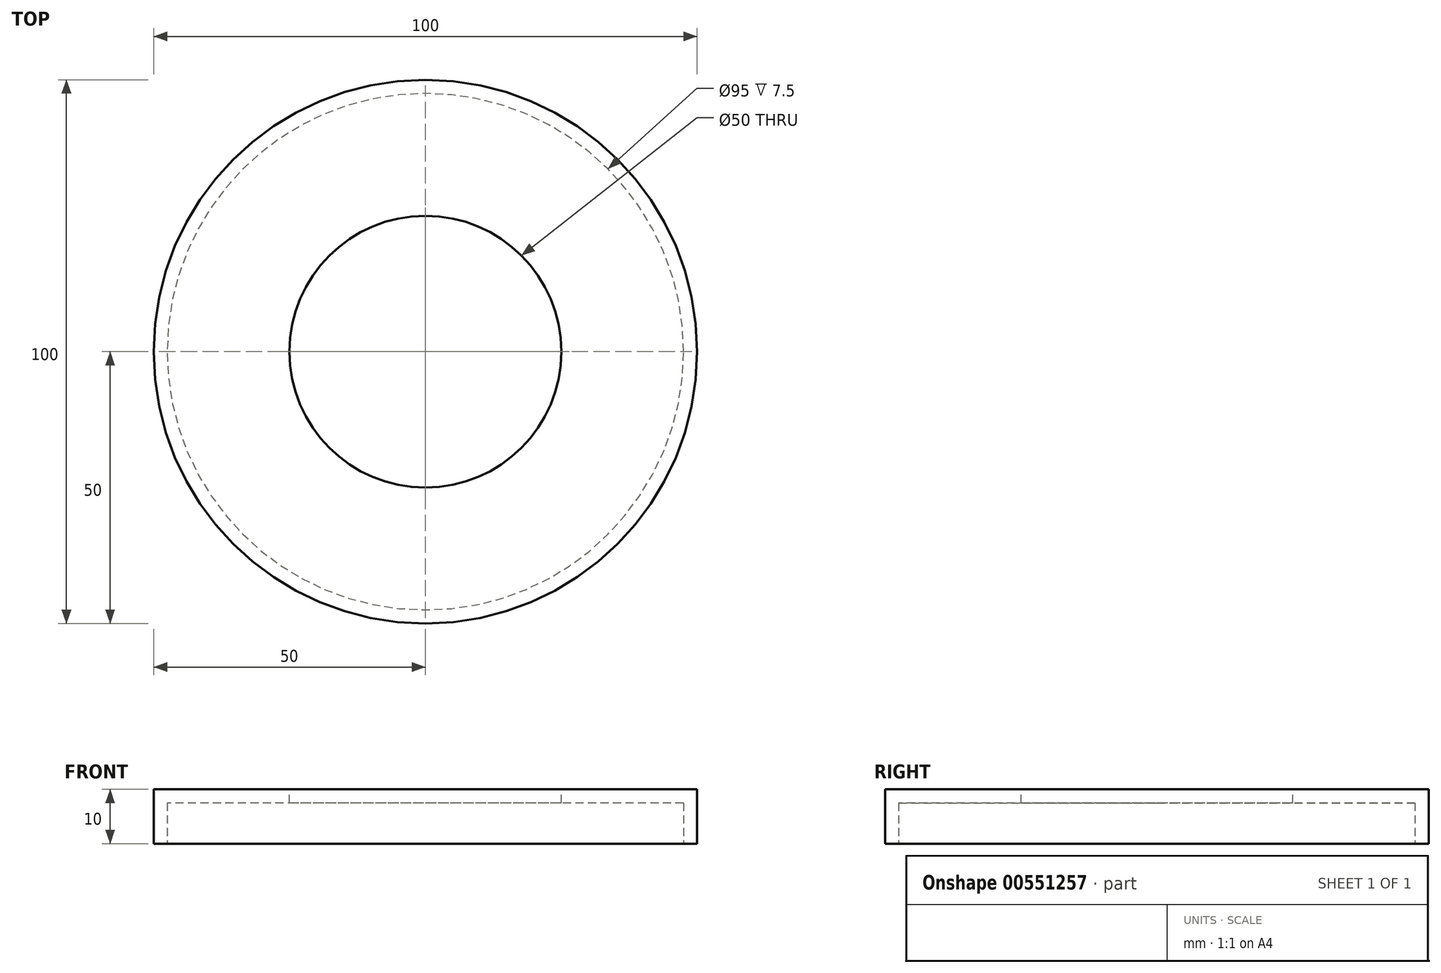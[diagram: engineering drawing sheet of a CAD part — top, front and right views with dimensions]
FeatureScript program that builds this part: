
annotation { "Feature Type Name" : "Feature", "Feature Type Description" : "" }
export const myFeature = defineFeature(function(context is Context, id is Id, definition is map)
    precondition{}
    {
        {
            var Q0;
            Q0=qCreatedBy(makeId("Top.planeOp"),FACE);
            var sketch = newSketch(context, id + "F0", { "sketchPlane" : qUnion([Q0])});
            skCircle(sketch, "E0", {"center": v(0, 0) * mm, "radius": 50 * mm});
            skSolve(sketch);
        }
        {
            var Q0;
            Q0=makeQuery(id+"F0.imprint","IMPRINT",FACE,{"disambiguationData":[TD([[makeQuery(id+"F0.imprint","IMPRINT",EDGE,{"derivedFrom":sQuery(id+"F0.wireOp",EDGE,"E0")}),1.0]])]});
            extrude(context, id + "F1", {"entities" : qUnion([Q0]), "depth" : 10 * mm, "offsetDistance" : 25 * mm});
        }
        {
            var Q0;
            Q0=makeQuery(id+"F1.opExtrude","CAP_FACE",FACE,{"disambiguationData":[OSD([sQuery(id+"F0.wireOp",EDGE,"E0")])],"isStart":true});
            shell(context, id + "F2", {"entities" : qUnion([Q0]), "thickness" : 2.5 * mm});
        }
        {
            var Q0;
            Q0=makeQuery(id+"F1.opExtrude","CAP_FACE",FACE,{"disambiguationData":[OSD([sQuery(id+"F0.wireOp",EDGE,"E0")])],"isStart":false});
            var sketch = newSketch(context, id + "F3", { "sketchPlane" : qUnion([Q0])});
            skCircle(sketch, "E1", {"center": v(0, 0) * mm, "radius": 25 * mm});
            skSolve(sketch);
        }
        {
            var Q0;
            Q0=makeQuery(id+"F3.imprint","IMPRINT",FACE,{"disambiguationData":[TD([[makeQuery(id+"F3.imprint","IMPRINT",EDGE,{"derivedFrom":sQuery(id+"F3.wireOp",EDGE,"E1")}),1.0]])]});
            extrude(context, id + "F4", {"entities" : qUnion([Q0]), "operationType" : NewBodyOperationType.REMOVE, "oppositeDirection" : true, "depth" : 25 * mm, "offsetDistance" : 25 * mm});
        }
    });
